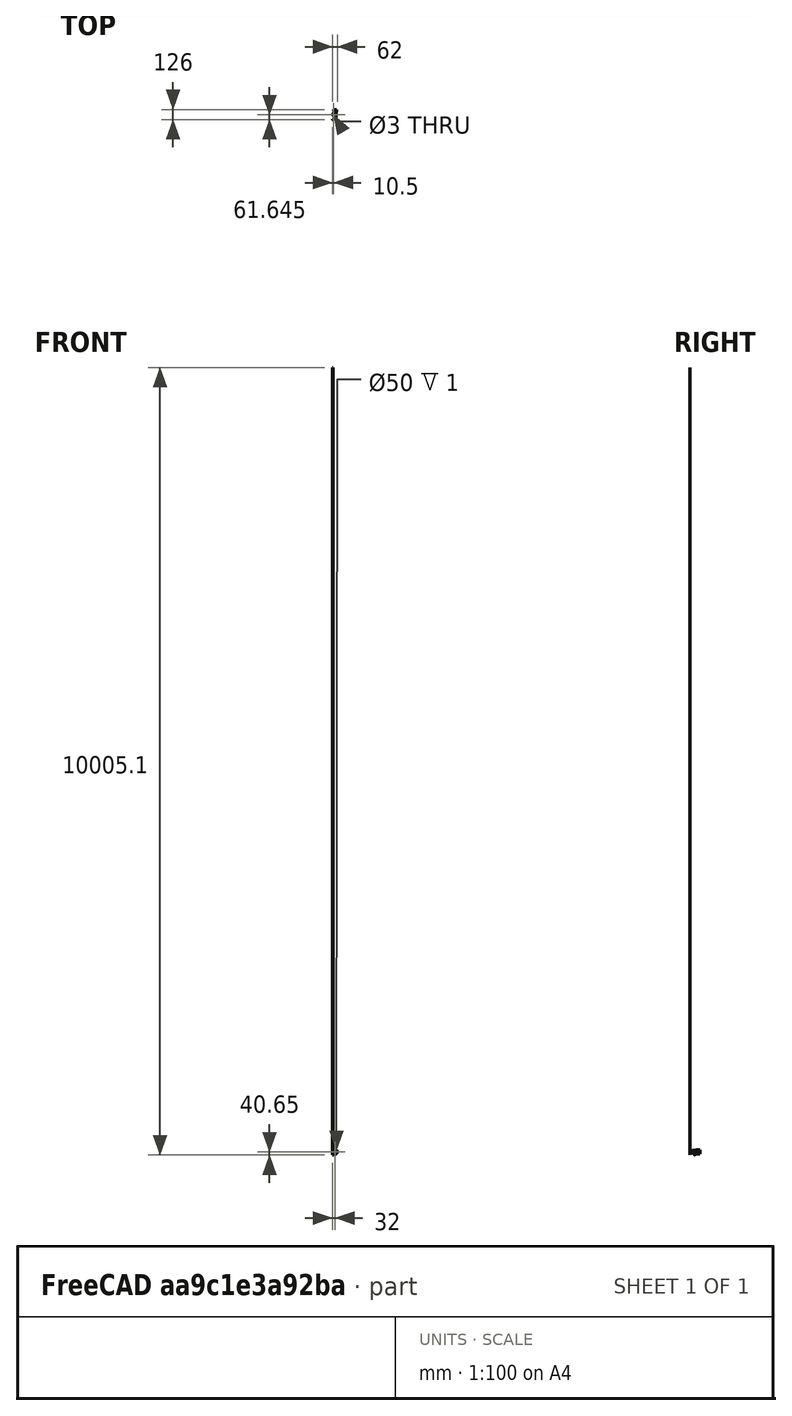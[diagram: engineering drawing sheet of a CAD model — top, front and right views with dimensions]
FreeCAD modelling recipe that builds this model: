
FCSTD DOCUMENT  (FreeCAD 0.16R6662 (Git))
Label: qtippholder-jw-csg
License: All rights reserved
LicenseURL: http://en.wikipedia.org/wiki/All_rights_reserved
objects: Part::Cylinder×7, Part::Box×6, Part::Cone×3, Part::MultiFuse×3, Part::Cut×3, Sketcher::SketchObject×2, App::DocumentObjectGroup×2, Mesh::Feature×1, PartDesign::Pad×1, Part::Sphere×1, PartDesign::Pocket×1
note: 29 computed .brp shape members not serialized (recipe doc carries the construction recipe); baked Part::Feature solids carry a one-line shape summary decoded from their .brp

FEATURE [Mesh::Feature] EarClnrHldr
  Placement = pos=(1.7939,1.69608,-3.31283) rot=(0,0,1;0rad)
FEATURE [Part::Box] Box  label="hut"
  Height = 50
  Length = 36
  Placement = pos=(14,116,11) rot=(0,0,1;0rad)
  Width = 10
FEATURE [Part::Box] Box001  label="stirn"
  Height = 46
  Length = 32
  Placement = pos=(16,102,13) rot=(0,0,1;0rad)
  Width = 17
FEATURE [Part::Box] Box002  label="gnack"
  Height = 10
  Length = 26
  Placement = pos=(22,92,31) rot=(0,0,1;0rad)
  Width = 12
FEATURE [Part::Box] Box003  label="augen"
  Height = 46
  Length = 26
  Placement = pos=(20,77,13) rot=(0,0,1;0rad)
  Width = 26
FEATURE [Part::Box] Box004  label="wangen"
  Height = 35
  Length = 22
  Placement = pos=(22,44,18) rot=(0,0,1;0rad)
  Width = 36
FEATURE [Part::Cylinder] Cylinder  label="kinn"
  Angle = 360
  Height = 18
  Placement = pos=(24,43,35.5) rot=(0,1,0;1.5708rad)
  Radius = 17.5
FEATURE [Sketcher::SketchObject] Sketch001
  Placement = pos=(22,44,36) rot=(0,0,1;0rad)
  sketch-geometry (10):
    g0: LineSegment StartX=1.5 StartY=7.67084 StartZ=0 EndX=-16.9205 EndY=7.67084 EndZ=0
    g1: LineSegment StartX=-20.1462 StartY=11.8885 StartZ=0 EndX=-17.1712 EndY=22.8519 EndZ=0
    g2: LineSegment StartX=-12.6256 StartY=34.6 StartZ=0 EndX=-6.24014 EndY=47.0658 EndZ=0
    g3: LineSegment StartX=-5.70418 StartY=49.2877 StartZ=0 EndX=-5.70418 EndY=58.874 EndZ=0
    g4: LineSegment StartX=-5.70418 StartY=58.874 StartZ=0 EndX=1.5 EndY=58.874 EndZ=0
    g5: LineSegment StartX=1.5 StartY=58.874 StartZ=0 EndX=1.5 EndY=7.67084 EndZ=0
    g6: ArcOfCircle CenterX=-16.9205 CenterY=11.0132 CenterZ=0 NormalX=0 NormalY=0 NormalZ=1 Radius=3.34236 StartAngle=2.87662 EndAngle=4.71239
    g7: ArcOfCircle CenterX=41.2664 CenterY=6.99453 CenterZ=0 NormalX=0 NormalY=0 NormalZ=1 Radius=60.5508 StartAngle=2.6682 EndAngle=2.87662
    g8: ArcOfCircle CenterX=-10.5778 CenterY=49.2877 CenterZ=0 NormalX=0 NormalY=0 NormalZ=1 Radius=4.87365 StartAngle=5.8098 EndAngle=6.28319
    g9: Circle CenterX=-11.5 CenterY=17.6445 CenterZ=0 NormalX=0 NormalY=0 NormalZ=1 Radius=1.5
  constraints (14):
    c: Horizontal(g0)
    c: Vertical(g3)
    c: Coincident(g3,g4)
    c: Horizontal(g4)
    c: Coincident(g4,g5)
    c: Coincident(g5,g0)
    c: Vertical(g5)
    c: Tangent(g0,g6) = 1.5708
    c: Tangent(g1,g6) = 1.5708
    c: Tangent(g1,g7) = 1.5708
    c: Tangent(g2,g7) = 1.5708
    c: Tangent(g2,g8) = -1.5708
    c: Tangent(g3,g8) = -1.5708
    c: Radius(g9) = 1.5
FEATURE [PartDesign::Pad] Pad  label="nase"
  Length = 4.5
  Length2 = 5.5
  Placement = pos=(22,44,36) rot=(0,0,1;0rad)
  Sketch = -> Sketch001
  Type = 4
FEATURE [Part::Cylinder] Cylinder002  label="bein006"
  Angle = 360
  Height = 32
  Placement = pos=(32,34,35.5) rot=(1,0,0;1.5708rad)
  Radius = 4
FEATURE [Part::Cylinder] Cylinder003  label="bein001"
  Angle = 360
  Height = 11
  Placement = pos=(32,12,35.5) rot=(1,0,0;1.5708rad)
  Radius = 5
FEATURE [Part::Cylinder] Cylinder004  label="bein002"
  Angle = 360
  Height = 4
  Placement = pos=(32,7,35.5) rot=(1,0,0;1.5708rad)
  Radius = 15
FEATURE [Part::Cylinder] Cylinder005  label="bein003"
  Angle = 360
  Height = 3
  Placement = pos=(32,5,35.5) rot=(1,0,0;1.5708rad)
  Radius = 30
FEATURE [Part::Cylinder] Cylinder006  label="bein004"
  Angle = 360
  Height = 3
  Placement = pos=(32,3,35.5) rot=(1,0,0;1.5708rad)
  Radius = 25
FEATURE [Part::Box] Box005  label="kopfloch"
  Height = 40
  Length = 26
  Placement = pos=(19,81,16) rot=(0,0,1;0rad)
  Width = 50
FEATURE [Part::Cylinder] Cylinder007  label="staebchen"
  Angle = 360
  Height = 27
  Placement = pos=(10.5,62,4) rot=(0,0,1;0rad)
  Radius = 2
FEATURE [Part::Sphere] Sphere  label="Kugel"
  Angle1 = -90
  Angle2 = 90
  Angle3 = 360
  Placement = pos=(10.5,62,-1) rot=(0,0,1;0rad)
  Radius = 4.15
FEATURE [Part::Cone] Cone  label="Kegel"
  Angle = 360
  Height = 10
  Placement = pos=(10.5,62,0) rot=(0,0,1;0rad)
  Radius1 = 4
  Radius2 = 2
FEATURE [Part::Cone] Cone001  label="Kegel001"
  Angle = 360
  Height = 5
  Placement = pos=(10.5,62,31) rot=(0,0,1;0rad)
  Radius1 = 2
  Radius2 = 1.8
FEATURE [Part::Cone] Cone002  label="beinloch001"
  Angle = 360
  Height = 11
  Placement = pos=(32,35,35.5) rot=(1,0,0;1.5708rad)
  Radius1 = 3.9
  Radius2 = 4.2
FEATURE [Part::MultiFuse] Fusion
  Shapes = -> [Box,Box001,Box002,Box003,Box004,Cylinder,Pad]
FEATURE [Part::Cut] Cut
  Base = -> Fusion
  Tool = -> Box005
FEATURE [Part::Cut] Cut001  label="kopf"
  Base = -> Cut
  Tool = -> Cone002
FEATURE [Part::MultiFuse] Fusion001
  Shapes = -> [Cone001,Cylinder007,Sphere,Cone]
FEATURE [App::DocumentObjectGroup] Gruppe001  label="halb-qtipp"
  Group = -> [Fusion001]
FEATURE [Part::MultiFuse] Fusion002
  Shapes = -> [Cylinder002,Cylinder003,Cylinder005,Cylinder004]
FEATURE [Part::Cut] Cut002
  Base = -> Fusion002
  Tool = -> Cylinder006
FEATURE [App::DocumentObjectGroup] Gruppe  label="bein"
  Group = -> [Cut002]
FEATURE [Sketcher::SketchObject] Sketch
  Placement = pos=(19,81,16) rot=(1,0,0;3.14159rad)
  Support = -> Box005 [Face5]
  sketch-geometry (4):
    g0: LineSegment StartX=0 StartY=0 StartZ=0 EndX=0 EndY=-2 EndZ=0
    g1: LineSegment StartX=0 StartY=-2 StartZ=0 EndX=2 EndY=-2 EndZ=0
    g2: LineSegment StartX=2 StartY=-2 StartZ=0 EndX=4 EndY=0 EndZ=0
    g3: LineSegment StartX=4 StartY=0 StartZ=0 EndX=0 EndY=0 EndZ=0
  constraints (11):
    c: Coincident(g-1,g0)
    c: PointOnObject(g0,g-2)
    c: Coincident(g0,g1)
    c: Horizontal(g1)
    c: Coincident(g1,g2)
    c: Coincident(g2,g3)
    c: Coincident(g3,g0)
    c: Horizontal(g3)
    c: DistanceY(g0,g0) = 2
    c: DistanceX(g1,g1) = 2
    c: DistanceX(g3,g3) = 4
FEATURE [PartDesign::Pocket] Pocket
  Length = 5
  Placement = pos=(19,81,16) rot=(0,0,1;0rad)
  Sketch = -> Sketch
  Type = 1
